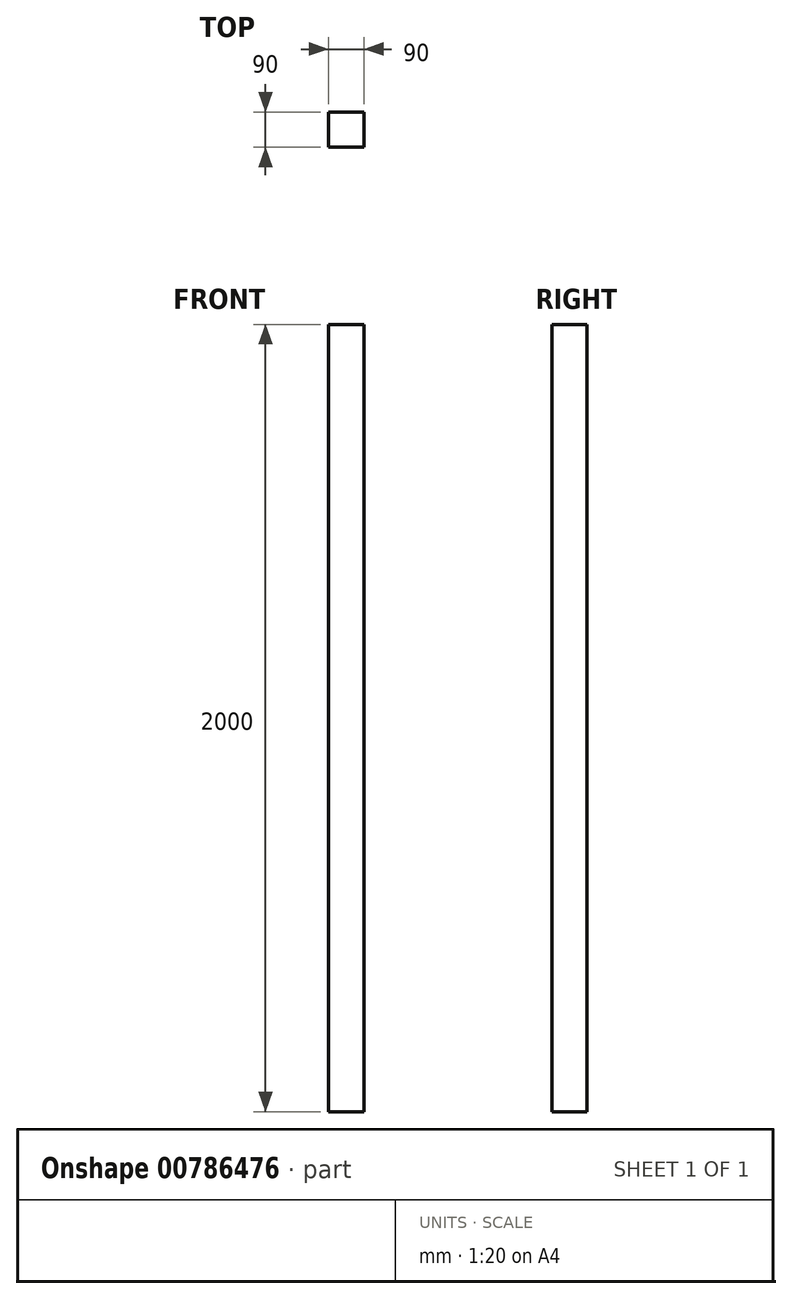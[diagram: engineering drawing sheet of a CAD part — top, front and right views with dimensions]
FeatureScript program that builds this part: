
annotation { "Feature Type Name" : "Feature", "Feature Type Description" : "" }
export const myFeature = defineFeature(function(context is Context, id is Id, definition is map)
    precondition{}
    {
        {
            var Q0;
            Q0=qCreatedBy(makeId("Top.planeOp"),FACE);
            var sketch = newSketch(context, id + "F0", { "sketchPlane" : qUnion([Q0])});
            skLineSegment(sketch, "E0.bottom", {"start": v(-45, 45) * mm, "end": v(45, 45) * mm});
            skLineSegment(sketch, "E0.top", {"start": v(-45, -45) * mm, "end": v(45, -45) * mm});
            skLineSegment(sketch, "E0.left", {"start": v(-45, 45) * mm, "end": v(-45, -45) * mm});
            skLineSegment(sketch, "E0.right", {"start": v(45, 45) * mm, "end": v(45, -45) * mm});
            skSolve(sketch);
        }
        {
            var Q0;
            Q0=makeQuery(id+"F0.imprint","IMPRINT",FACE,{"disambiguationData":[TD([[makeQuery(id+"F0.imprint","IMPRINT",EDGE,{"derivedFrom":sQuery(id+"F0.wireOp",EDGE,"E0.bottom")}),-1.0]])]});
            extrude(context, id + "F1", {"entities" : qUnion([Q0]), "depth" : 2000 * mm, "offsetDistance" : 25 * mm});
        }
    });
